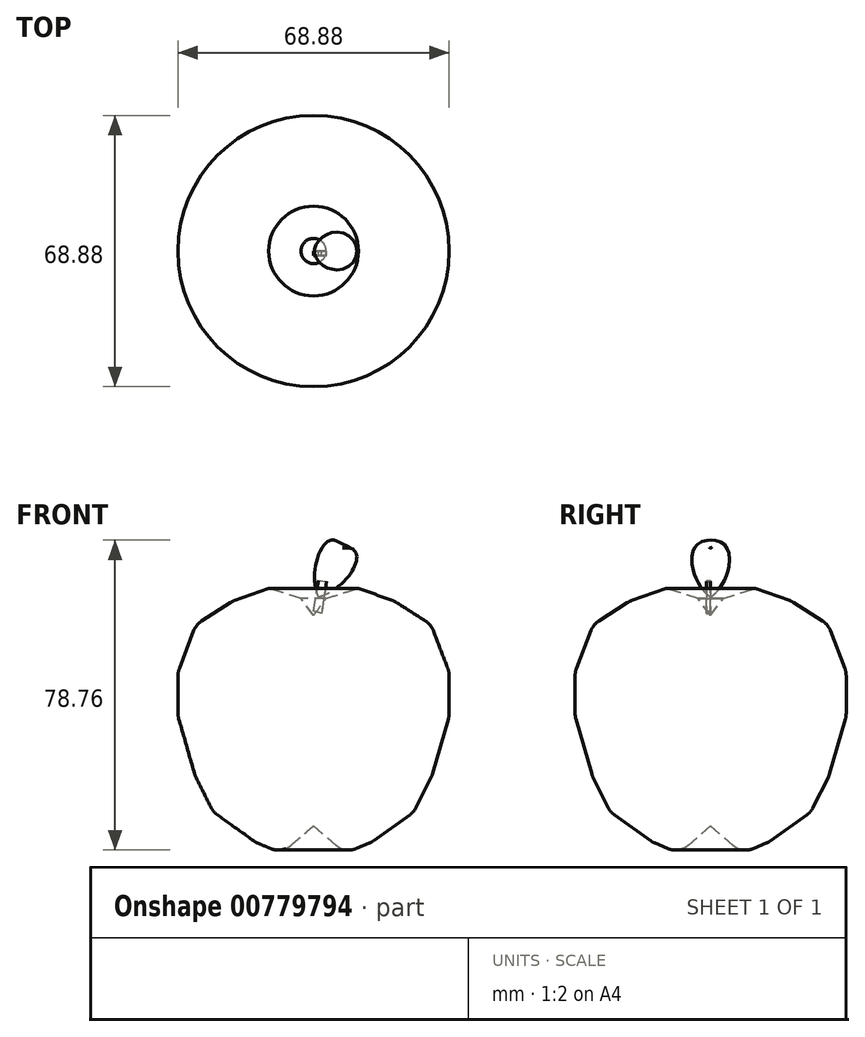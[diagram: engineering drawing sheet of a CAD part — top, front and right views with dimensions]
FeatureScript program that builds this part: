
annotation { "Feature Type Name" : "Feature", "Feature Type Description" : "" }
export const myFeature = defineFeature(function(context is Context, id is Id, definition is map)
    precondition{}
    {
        {
            var Q0;
            Q0=qCreatedBy(makeId("Front.planeOp"),FACE);
            var sketch = newSketch(context, id + "F0", { "sketchPlane" : qUnion([Q0])});
            skLineSegment(sketch, "E0", {"start": v(0, 22.27) * mm, "end": v(0, -30.72) * mm});
            skLineSegment(sketch, "E1", {"start": v(0, -30.72) * mm, "end": v(-6.27, -35.59) * mm});
            skLineSegment(sketch, "E2", {"start": v(-6.27, -35.59) * mm, "end": v(-20.87, -26.88) * mm});
            skLineSegment(sketch, "E3", {"start": v(-20.87, -26.88) * mm, "end": v(-31.88, -6.4) * mm});
            skLineSegment(sketch, "E4", {"start": v(-31.88, -6.4) * mm, "end": v(-31.88, 10.75) * mm});
            skLineSegment(sketch, "E5", {"start": v(-31.88, 10.75) * mm, "end": v(-21.63, 20.23) * mm});
            skLineSegment(sketch, "E6", {"start": v(-21.63, 20.23) * mm, "end": v(-8.32, 30.47) * mm});
            skLineSegment(sketch, "E7", {"start": v(-8.32, 30.47) * mm, "end": v(0, 22.27) * mm});
            skSolve(sketch);
        }
        {
            var Q0;
            Q0=makeQuery(id+"F0.imprint","IMPRINT",FACE,{"disambiguationData":[TD([[makeQuery(id+"F0.imprint","IMPRINT",EDGE,{"derivedFrom":sQuery(id+"F0.wireOp",EDGE,"E0")}),-1.0]])]});
            var Q1;
            Q1=sQuery(id+"F0.wireOp",EDGE,"E0");
            revolve(context, id + "F1", {"surfaceOperationType" : NewSurfaceOperationType.NEW, "entities" : qUnion([Q0]), "axis" : qUnion([Q1]), "revolveType" : RevolveType.FULL});
        }
        {
            var Q0;
            Q0=makeQuery(id+"F1.opRevolve","SWEPT_FACE",FACE,{"disambiguationData":[OSD([sQuery(id+"F0.wireOp",EDGE,"E3")])]});
            var Q1;
            Q1=makeQuery(id+"F1.opRevolve","SWEPT_FACE",FACE,{"disambiguationData":[OSD([sQuery(id+"F0.wireOp",EDGE,"E5")])]});
            var Q2;
            Q2=makeQuery(id+"F1.opRevolve","SWEPT_FACE",FACE,{"disambiguationData":[OSD([sQuery(id+"F0.wireOp",EDGE,"E6")])]});
            var Q3;
            Q3=makeQuery(id+"F1.opRevolve","SWEPT_FACE",FACE,{"disambiguationData":[OSD([sQuery(id+"F0.wireOp",EDGE,"E2")])]});
            fillet(context, id + "F2", {"entities" : qUnion([Q0, Q1, Q2, Q3]), "radius" : 4.82 * mm, "tangentPropagation" : true, "allowEdgeOverflow" : false});
        }
        {
            var Q0;
            Q0=makeQuery(id+"F1.opRevolve","SWEPT_BODY",BODY,{"disambiguationData":[OSD([sQuery(id+"F0.wireOp",EDGE,"E0"),sQuery(id+"F0.wireOp",EDGE,"E1"),sQuery(id+"F0.wireOp",EDGE,"E2"),sQuery(id+"F0.wireOp",EDGE,"E3"),sQuery(id+"F0.wireOp",EDGE,"E4"),sQuery(id+"F0.wireOp",EDGE,"E5"),sQuery(id+"F0.wireOp",EDGE,"E6"),sQuery(id+"F0.wireOp",EDGE,"E7")])]});
            deleteBodies(context, id + "F3", {"entities" : qUnion([Q0])});
        }
        {
            var Q0;
            Q0=qCreatedBy(makeId("Front.planeOp"),FACE);
            var sketch = newSketch(context, id + "F4", { "sketchPlane" : qUnion([Q0])});
            skLineSegment(sketch, "E8", {"start": v(0, 22.53) * mm, "end": v(0, -30.98) * mm});
            skLineSegment(sketch, "E9", {"start": v(0, -30.98) * mm, "end": v(-8.07, -37.9) * mm});
            skLineSegment(sketch, "E10", {"start": v(-8.07, -37.9) * mm, "end": v(-14.72, -35.08) * mm});
            skLineSegment(sketch, "E11", {"start": v(-14.72, -35.08) * mm, "end": v(-25.48, -27.4) * mm});
            skLineSegment(sketch, "E12", {"start": v(-25.48, -27.4) * mm, "end": v(-30.08, -18.18) * mm});
            skLineSegment(sketch, "E13", {"start": v(-30.08, -18.18) * mm, "end": v(-34.44, -3.07) * mm});
            skLineSegment(sketch, "E14", {"start": v(-34.44, -3.07) * mm, "end": v(-34.44, 8.2) * mm});
            skLineSegment(sketch, "E15", {"start": v(-34.44, 8.2) * mm, "end": v(-29.83, 20.23) * mm});
            skLineSegment(sketch, "E16", {"start": v(-29.83, 20.23) * mm, "end": v(-20.61, 26.12) * mm});
            skLineSegment(sketch, "E17", {"start": v(-20.61, 26.12) * mm, "end": v(-11.4, 29.44) * mm});
            skLineSegment(sketch, "E18", {"start": v(-11.4, 29.44) * mm, "end": v(-3.2, 26.88) * mm});
            skLineSegment(sketch, "E19", {"start": v(-3.2, 26.88) * mm, "end": v(0, 22.53) * mm});
            skPoint(sketch, "E20.orphan", {"position": v(0, 40.7) * mm});
            skSolve(sketch);
        }
        {
            var Q0;
            Q0=makeQuery(id+"F4.imprint","IMPRINT",FACE,{"disambiguationData":[TD([[makeQuery(id+"F4.imprint","IMPRINT",EDGE,{"derivedFrom":sQuery(id+"F4.wireOp",EDGE,"E8")}),-1.0]])]});
            var Q1;
            Q1=sQuery(id+"F4.wireOp",EDGE,"E8");
            revolve(context, id + "F5", {"surfaceOperationType" : NewSurfaceOperationType.NEW, "entities" : qUnion([Q0]), "axis" : qUnion([Q1]), "revolveType" : RevolveType.FULL});
        }
        {
            var Q0;
            Q0=makeQuery(id+"F5.opRevolve","SWEPT_FACE",FACE,{"disambiguationData":[OSD([sQuery(id+"F4.wireOp",EDGE,"E16")])]});
            var Q1;
            Q1=makeQuery(id+"F5.opRevolve","SWEPT_FACE",FACE,{"disambiguationData":[OSD([sQuery(id+"F4.wireOp",EDGE,"E15")])]});
            var Q2;
            Q2=makeQuery(id+"F5.opRevolve","SWEPT_FACE",FACE,{"disambiguationData":[OSD([sQuery(id+"F4.wireOp",EDGE,"E14")])]});
            var Q3;
            Q3=makeQuery(id+"F5.opRevolve","SWEPT_FACE",FACE,{"disambiguationData":[OSD([sQuery(id+"F4.wireOp",EDGE,"E13")])]});
            var Q4;
            Q4=makeQuery(id+"F5.opRevolve","SWEPT_FACE",FACE,{"disambiguationData":[OSD([sQuery(id+"F4.wireOp",EDGE,"E12")])]});
            var Q5;
            Q5=makeQuery(id+"F5.opRevolve","SWEPT_FACE",FACE,{"disambiguationData":[OSD([sQuery(id+"F4.wireOp",EDGE,"E11")])]});
            var Q6;
            Q6=makeQuery(id+"F5.opRevolve","SWEPT_FACE",FACE,{"disambiguationData":[OSD([sQuery(id+"F4.wireOp",EDGE,"E10")])]});
            fillet(context, id + "F6", {"entities" : qUnion([Q0, Q1, Q2, Q3, Q4, Q5, Q6]), "radius" : 5.08 * mm, "tangentPropagation" : true, "allowEdgeOverflow" : false});
        }
        {
            var Q0;
            Q0=qCreatedBy(makeId("Front.planeOp"),FACE);
            var sketch = newSketch(context, id + "F7", { "sketchPlane" : qUnion([Q0])});
            skLineSegment(sketch, "E21", {"start": v(0, 24.88) * mm, "end": v(4.29, 33.44) * mm});
            skEllipse(sketch, "E22", {"center": v(4.29, 33.44) * mm, "majorRadius": 8.28 * mm, "minorRadius": 4 * mm, "majorAxis": v(0.74, 0.67)});
            skLineSegment(sketch, "E23", {"start": v(0, 24.88) * mm, "end": v(7.38, 39.62) * mm});
            skSolve(sketch);
        }
        {
            var Q0;
            {var subQ3=sQuery(id+"F7.wireOp",EDGE,"E23");Q0=makeQuery(id+"F7.imprint","IMPRINT",FACE,{"disambiguationData":[TD([[makeQuery(id+"F7.imprint","IMPRINT",EDGE,{"derivedFrom":subQ3}),-1.0]])]});}
            var Q1;
            Q1=sQuery(id+"F7.wireOp",EDGE,"E23");
            revolve(context, id + "F8", {"surfaceOperationType" : NewSurfaceOperationType.NEW, "entities" : qUnion([Q0]), "axis" : qUnion([Q1]), "revolveType" : RevolveType.FULL});
        }
        {
            var Q0;
            Q0=qCreatedBy(makeId("Front.planeOp"),FACE);
            var sketch = newSketch(context, id + "F9", { "sketchPlane" : qUnion([Q0])});
            skLineSegment(sketch, "E24", {"start": v(0, 23.64) * mm, "end": v(1.25, 31.48) * mm});
            skLineSegment(sketch, "E25", {"start": v(1.25, 31.48) * mm, "end": v(3.32, 31.15) * mm});
            skLineSegment(sketch, "E26", {"start": v(3.32, 31.15) * mm, "end": v(2.03, 23.04) * mm});
            skLineSegment(sketch, "E27", {"start": v(2.03, 23.04) * mm, "end": v(0, 23.64) * mm});
            skSolve(sketch);
        }
        {
            var Q0;
            Q0=makeQuery(id+"F9.imprint","IMPRINT",FACE,{"disambiguationData":[TD([[makeQuery(id+"F9.imprint","IMPRINT",EDGE,{"derivedFrom":sQuery(id+"F9.wireOp",EDGE,"E24")}),-1.0]])]});
            extrude(context, id + "F10", {"entities" : qUnion([Q0]), "depth" : 1.12 * mm, "offsetDistance" : 25.4 * mm});
        }
    });
